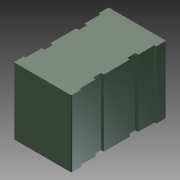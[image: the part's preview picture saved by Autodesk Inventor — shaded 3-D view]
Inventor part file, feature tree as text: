
AUTODESK INVENTOR PART (.ipt)
format: ipt  version: 2014 (Build 180170000, 170)  size: 161,280 bytes
history: native  units: in
note: dims shown in document units (in); Inventor stores cm internally (conversion verified against a paired STEP export)
features: other x21, extrude x3, sketch x3, pattern_linear x1
ambient origin geometry x8: Origin, YZ Plane, XZ Plane, XY Plane, X Axis, Y Axis, Z Axis, Center Point
bodies: Solid1 (feature_tree)
feature tree (28):
  extrude  "Extrusion1"  Depth=0.001in TaperAngle=0.0deg
  extrude  "Extrusion2"  Depth=0.185in TaperAngle=0.0deg
  extrude  "Extrusion3"  [1 undecoded]
  pattern_linear  "Rectangular Pattern1"  [2 undecoded]
  other  "rot_XY"
  other  "rot_YZ"
  other  "rot_ZX"
  other  "rot_X"
  other  "rot_Y"
  other  "rot_Z"
  other  "rot_Center"
  other  "to_cover_XY"
  other  "to_cover_YZ"
  other  "to_cover_ZX"
  other  "to_cover_X"
  other  "to_cover_Y"
  other  "to_cover_Z"
  other  "to_cover_Center"
  other  "to_terminals_XY"
  other  "to_terminals_YZ"
  other  "to_terminals_ZX"
  other  "to_terminals_X"
  other  "to_terminals_Y"
  other  "to_terminals_Z"
  other  "to_terminals_Center"
  sketch  "Sketch_2"  dims[d4=0.01in d5=0.0in d6=1.1811in d8=0.185in d9=0.3937in d11=0.0in]
  sketch  "Sketch_1"  dims[d0=0.361in d1=0.0in d2=0.001in d3=0.0in]
  sketch  "Sketch_7"
note: 3 required parameter values undecoded (feature->parameter linkage not recoverable at this tier; creation-order binding heuristic only, values carry confidence <= 0.55)
